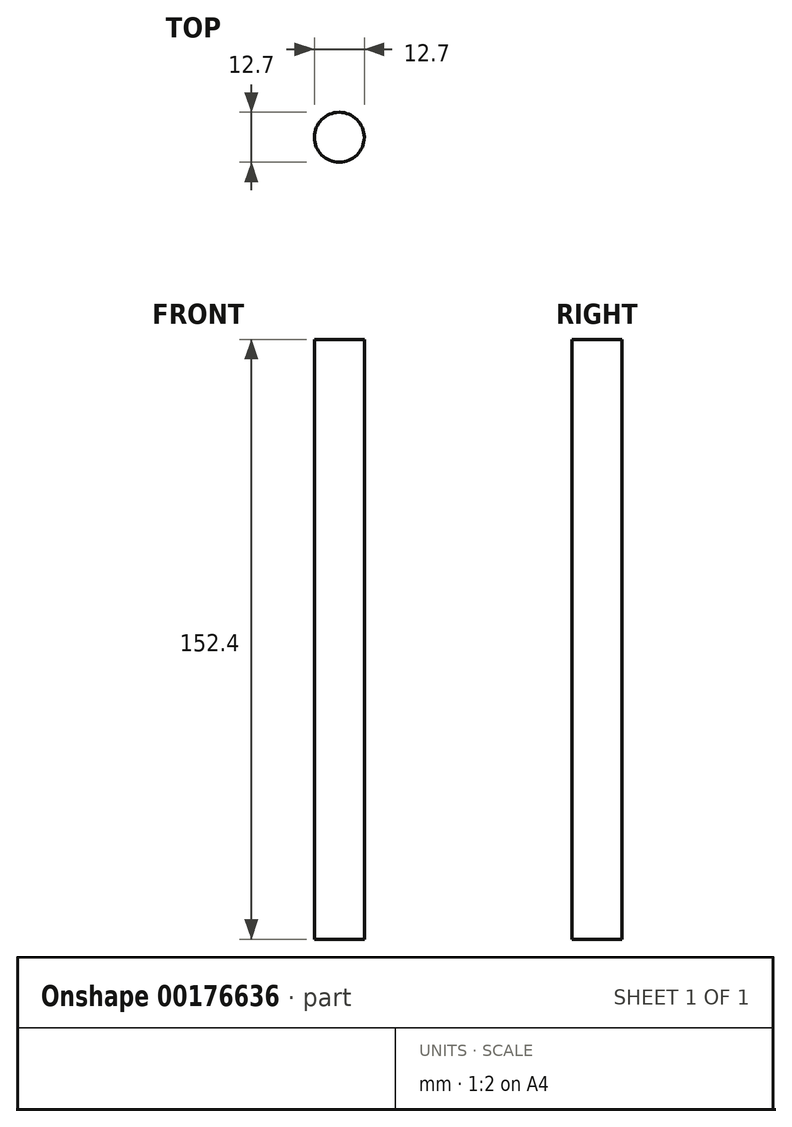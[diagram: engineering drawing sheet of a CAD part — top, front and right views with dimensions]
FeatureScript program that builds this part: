
annotation { "Feature Type Name" : "Feature", "Feature Type Description" : "" }
export const myFeature = defineFeature(function(context is Context, id is Id, definition is map)
    precondition{}
    {
        {
            var Q0;
            Q0=qCreatedBy(makeId("Top.planeOp"),FACE);
            var sketch = newSketch(context, id + "F0", { "sketchPlane" : qUnion([Q0])});
            skCircle(sketch, "E0", {"center": v(0, 0) * mm, "radius": 6.35 * mm});
            skSolve(sketch);
        }
        {
            var Q0;
            Q0=makeQuery(id+"F0.imprint","IMPRINT",FACE,{"disambiguationData":[TD([[makeQuery(id+"F0.imprint","IMPRINT",EDGE,{"derivedFrom":sQuery(id+"F0.wireOp",EDGE,"E0")}),1.0]])]});
            extrude(context, id + "F1", {"entities" : qUnion([Q0]), "depth" : 152.4 * mm});
        }
    });
